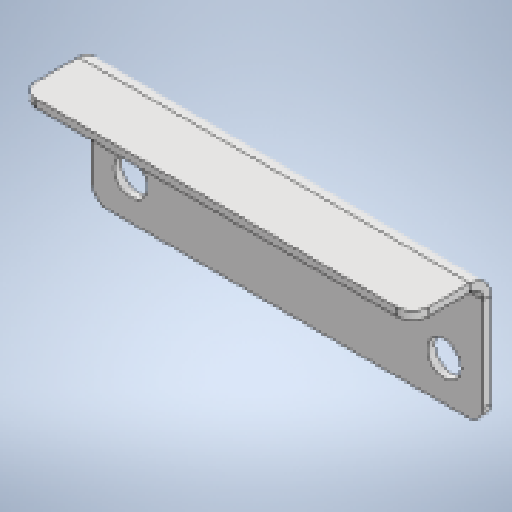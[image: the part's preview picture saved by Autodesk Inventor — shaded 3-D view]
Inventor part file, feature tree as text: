
AUTODESK INVENTOR PART (.ipt)
format: ipt  version: 2025.1 (Build 291241020, 241B)  size: 306,688 bytes
history: native  units: mm
features: sheet_metal_op x4, other x4, sketch x3, chamfer x1
ambient origin geometry x8: Origin, YZ Plane, XZ Plane, XY Plane, X Axis, Y Axis, Z Axis, Center Point
bodies: Body1 (feature_tree)
feature tree (12):
  sheet_metal_op  "Face2"
  sheet_metal_op  "Flange1"
  chamfer  "Corner Round6"
  sketch  "Sketch4"  dims[d36=150.0mm]
  other  "Plate2"
  sketch  "Sketch5"  dims[d37=50.0mm]
  sketch  "Sketch6"  dims[d38=3.0mm d39=120.0mm d40=15.0mm d41=13.0mm d42=3.0mm d43=0.0mm d44=3.0mm d45=1.5mm d46=6.0mm d47=5.0mm d48=30.0mm d49=90.0deg d50=5.0mm d51=12.0mm d52=3.0mm d53=5.0mm d54=6.0mm]
  other  "Plate3"
  sheet_metal_op  "Bend1"
  sheet_metal_op  "Corner1"
  other  "Cut1"
  other  "Definition1"
